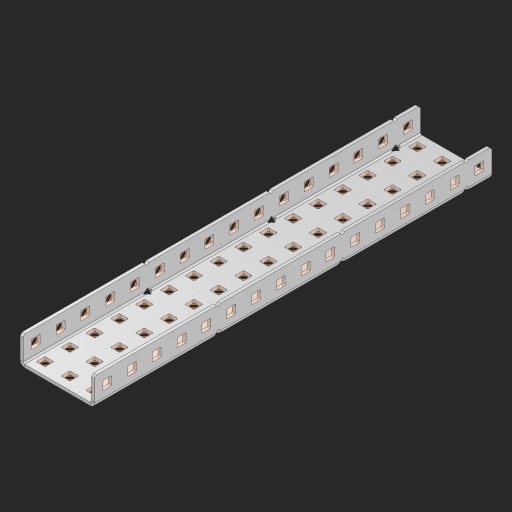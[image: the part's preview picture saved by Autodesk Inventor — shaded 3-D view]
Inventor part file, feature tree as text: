
AUTODESK INVENTOR PART (.ipt)
format: ipt  version: 2023 (Build 270158000, 158)  size: 1,206,272 bytes
history: native  units: in
note: dims shown in document units (in); Inventor stores cm internally (conversion verified against a paired STEP export)
features: other x85, extrude x79, sheet_metal_op x10, sketch x8, mirror x1, pattern_linear x1, chamfer x1
ambient origin geometry x8: Origin, YZ Plane, XZ Plane, XY Plane, X Axis, Y Axis, Z Axis, Center Point
bodies: Solid1 (feature_tree), Body (feature_tree)
feature tree (185):
  other  "Flange Pattern Plane"
  sheet_metal_op  "Flange Pattern"
  sheet_metal_op  "Body Pattern"
  other  "Arc Length"
  mirror  "Notch Mirror"
  pattern_linear  "Notch Pattern"  Spacing1=0.25in  [1 undecoded]
  chamfer  "End Chamfer"
  extrude  "Half Cut"  Depth=0.0625in
  sketch  "Sketch1"  dims[d0=1.5in]
  other  "Plate1"
  sketch  "Sketch2"  dims[d1=8.0in]
  other  "Plate2"
  sheet_metal_op  "Bend1"
  sheet_metal_op  "Corner1"
  sketch  "Sketch3"  dims[d2=0.0625in]
  other  "Flange Pattern Sketch"
  sketch  "Sketch7"  dims[d3=0.0625in]
  other  "Srf1"
  other  "Srf2"
  sketch  "Sketch8"  dims[d4=0.0312in]
  sketch  "Sketch9"  dims[d5=0.125in]
  other  "Srf91"
  sheet_metal_op  "Body Pattern Sketch"
  other  "Srf92"
  sketch  "Sketch13"  dims[d6=0.0625in]
  sketch  "Sketch14"  dims[d7=0.5in d8=90.0deg d9=0.0312in d10=0.25in d11=0.0625in d12=0.0625in d16=0.182in d17=0.02in d18=0.0625in d19=0.0in d20=0.25in d21=0.25in d46=0.172in d47=1.0in d48=0.0in d49=0.182in d50=0.02in d51=0.25in d52=0.25in d53=0.0625in d54=0.0in d55=0.172in d56=1.0in d57=0.0in d60=6.2992in d62=0.5in d63=1.1811in d65=0.5in d85=0.1473in d86=0.1782in d88=0.04in d89=0.0625in d90=0.0in d91=0.04in d92=0.0491in d95=2.5in d96=0.04in d97=0.25in d98=45.0deg d101=0.0in d102=2.497in d131=1.5in d132=6.2992in d134=0.5in d139=0.5in]
  other  "Srf856"
  other  "Srf1310"
  other  "Srf1311"
  other  "Srf1312"
  other  "Srf1376"
  other  "Srf1377"
  other  "Srf1728"
  other  "Srf1755"
  other  "Srf1878"
  other  "Srf1879"
  other  "Srf1880"
  other  "Srf1881"
  other  "Srf1882"
  other  "Srf1883"
  other  "Srf1884"
  other  "Srf1885"
  other  "Srf1886"
  other  "Srf1887"
  other  "Srf1888"
  other  "Srf1889"
  other  "Srf1890"
  other  "Srf1891"
  other  "Srf1892"
  other  "Srf1893"
  other  "Srf1894"
  other  "Srf1895"
  other  "Srf1896"
  other  "Srf1897"
  other  "Srf1898"
  other  "Srf1899"
  other  "Srf1900"
  other  "Srf1901"
  other  "Srf1902"
  other  "Srf1903"
  other  "Srf1942"
  other  "Srf1943"
  other  "Srf1944"
  other  "Srf1945"
  other  "Srf1946"
  other  "Srf1947"
  other  "Srf1948"
  other  "Srf1949"
  other  "Srf1950"
  other  "Srf1951"
  other  "Srf1952"
  other  "Srf1953"
  other  "Srf1954"
  other  "Srf1955"
  other  "Srf1956"
  other  "Srf1957"
  other  "Srf1958"
  other  "Srf1959"
  other  "Srf1960"
  other  "Srf1961"
  other  "Srf1962"
  other  "Srf1963"
  other  "Srf1964"
  other  "Srf1965"
  other  "Srf1966"
  other  "Srf1967"
  other  "Srf1968"
  other  "Srf1969"
  other  "Srf1970"
  other  "Srf1971"
  other  "Srf1972"
  other  "Srf1973"
  other  "Srf1974"
  other  "Srf1975"
  other  "Srf1976"
  other  "Srf1977"
  other  "Srf1978"
  other  "Srf1979"
  other  "Srf1980"
  other  "Srf1981"
  other  "Srf1982"
  other  "Srf1983"
  sheet_metal_op  "Flange Stamp"
  sheet_metal_op  "Flange Circle"
  sheet_metal_op  "Body Stamp"
  sheet_metal_op  "Body Circle"
  sheet_metal_op  "Notch"
  extrude  "ExtrusionSrf2"  Depth=0.0625in
  extrude  "ExtrusionSrf92"  Depth=1.5in
  extrude  "ExtrusionSrf856"  Depth=0.02in
  extrude  "ExtrusionSrf1310"  Depth=0.0625in
  extrude  "ExtrusionSrf1311"  TaperAngle=0.0deg  [1 undecoded]
  extrude  "ExtrusionSrf1312"  Depth=0.25in
  extrude  "ExtrusionSrf1376"  Depth=0.25in
  extrude  "ExtrusionSrf1377"  Depth=1.5in
  extrude  "ExtrusionSrf1728"  Depth=1.5in TaperAngle=0.0deg
  extrude  "ExtrusionSrf1755"  Depth=1.5in
  extrude  "ExtrusionSrf1878"  Depth=0.02in
  extrude  "ExtrusionSrf1879"  Depth=0.25in
  extrude  "ExtrusionSrf1880"  Depth=0.25in
  extrude  "ExtrusionSrf1881"  Depth=0.0625in
  extrude  "ExtrusionSrf1882"  TaperAngle=0.0deg  [1 undecoded]
  extrude  "ExtrusionSrf1883"  Depth=1.5in
  extrude  "ExtrusionSrf1884"  Depth=1.5in TaperAngle=0.0deg
  extrude  "ExtrusionSrf1885"  Depth=1.5in
  extrude  "ExtrusionSrf1886"  Depth=1.5in
  extrude  "ExtrusionSrf1887"  Depth=1.5in
  extrude  "ExtrusionSrf1888"  Depth=1.5in
  extrude  "ExtrusionSrf1889"  Depth=1.5in
  extrude  "ExtrusionSrf1890"  Depth=0.0625in
  extrude  "ExtrusionSrf1891"  TaperAngle=0.0deg  [1 undecoded]
  extrude  "ExtrusionSrf1892"  Depth=1.5in
  extrude  "ExtrusionSrf1893"  Depth=1.5in
  extrude  "ExtrusionSrf1894"  Depth=1.5in
  extrude  "ExtrusionSrf1895"  Depth=0.25in TaperAngle=45.0deg
  extrude  "ExtrusionSrf1896"  TaperAngle=0.0deg  [1 undecoded]
  extrude  "ExtrusionSrf1897"  Depth=1.5in
  extrude  "ExtrusionSrf1898"  Depth=1.5in
  extrude  "ExtrusionSrf1899"  Depth=1.5in
  extrude  "ExtrusionSrf1900"  Depth=1.5in
  extrude  "ExtrusionSrf1901"  Depth=1.5in
  extrude  "ExtrusionSrf1902"  [1 undecoded]
  extrude  "ExtrusionSrf1903"  [1 undecoded]
  extrude  "ExtrusionSrf1942"  [1 undecoded]
  extrude  "ExtrusionSrf1943"  [1 undecoded]
  extrude  "ExtrusionSrf1944"  [1 undecoded]
  extrude  "ExtrusionSrf1945"  [1 undecoded]
  extrude  "ExtrusionSrf1946"  [1 undecoded]
  extrude  "ExtrusionSrf1947"  [1 undecoded]
  extrude  "ExtrusionSrf1948"  [1 undecoded]
  extrude  "ExtrusionSrf1949"  [1 undecoded]
  extrude  "ExtrusionSrf1950"  [1 undecoded]
  extrude  "ExtrusionSrf1951"  [1 undecoded]
  extrude  "ExtrusionSrf1952"  [1 undecoded]
  extrude  "ExtrusionSrf1953"  [1 undecoded]
  extrude  "ExtrusionSrf1954"  [1 undecoded]
  extrude  "ExtrusionSrf1955"  [1 undecoded]
  extrude  "ExtrusionSrf1956"  [1 undecoded]
  extrude  "ExtrusionSrf1957"  [1 undecoded]
  extrude  "ExtrusionSrf1958"  [1 undecoded]
  extrude  "ExtrusionSrf1959"  [1 undecoded]
  extrude  "ExtrusionSrf1960"  [1 undecoded]
  extrude  "ExtrusionSrf1961"  [1 undecoded]
  extrude  "ExtrusionSrf1962"  [1 undecoded]
  extrude  "ExtrusionSrf1963"  [1 undecoded]
  extrude  "ExtrusionSrf1964"  [1 undecoded]
  extrude  "ExtrusionSrf1965"  [1 undecoded]
  extrude  "ExtrusionSrf1966"  [1 undecoded]
  extrude  "ExtrusionSrf1967"  [1 undecoded]
  extrude  "ExtrusionSrf1968"  [1 undecoded]
  extrude  "ExtrusionSrf1969"  [1 undecoded]
  extrude  "ExtrusionSrf1970"  [1 undecoded]
  extrude  "ExtrusionSrf1971"  [1 undecoded]
  extrude  "ExtrusionSrf1972"  [1 undecoded]
  extrude  "ExtrusionSrf1973"  [1 undecoded]
  extrude  "ExtrusionSrf1974"  [1 undecoded]
  extrude  "ExtrusionSrf1975"  [1 undecoded]
  extrude  "ExtrusionSrf1976"  [1 undecoded]
  extrude  "ExtrusionSrf1977"  [1 undecoded]
  extrude  "ExtrusionSrf1978"  [1 undecoded]
  extrude  "ExtrusionSrf1979"  [1 undecoded]
  extrude  "ExtrusionSrf1980"  [1 undecoded]
  extrude  "ExtrusionSrf1981"  [1 undecoded]
  extrude  "ExtrusionSrf1982"  [1 undecoded]
  extrude  "ExtrusionSrf1983"  [1 undecoded]
note: 49 required parameter values undecoded (feature->parameter linkage not recoverable at this tier; creation-order binding heuristic only, values carry confidence <= 0.55)
